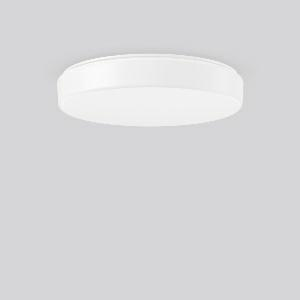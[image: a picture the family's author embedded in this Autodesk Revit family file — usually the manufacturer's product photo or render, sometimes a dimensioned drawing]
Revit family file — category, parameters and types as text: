
# Revit family: flat_polymero_kreis_672392_002_1_ad0b
name_source: partatom
category: Lighting Fixtures
units: mm (PartAtom-declared; Revit-internal decimal feet)

## family parameters
Cut with Voids When Loaded = No
Host = Face
Light Source = No
Part Type = Normal
Room Calculation Point = No
Round Connector Dimension = Use Diameter
Shared = No

## types (1)
- FLAT POLYMERO KREIS (1 x LED Modul 840, 2600 lm, 4000)
    Apparent Load = 23 VA
    CIE Flux Codes = 42 72 91 84 100
    Color Rendering = 80
    Color Temperature = 4000
    Default Elevation = 1800 mm
    Description = Series: FLAT POLYMERO KREIS
Decorative round surface-mounted luminaire. For escape route illumination. Base: metal, powder-coated. Diffuser made of non-yellowing plastic (PMMA), opal. Diffuser fastening: patented push system. Suitable for Ceiling mounting, Wall (surface). Driver integrated. Suitable for connection to central battery systems. 
Colour: white
Diameter: 515 mm
Height: 98 mm
Weight: 2.8 kg
Operating mode: Combined NL readiness
Lamp: LED
Socket: without socket
Colour temperature: 4000K
Colour rendering index (CRI): 80
System power: 23 W
Rated luminous flux: 2600 lm
Luminous flux, emergency: 550 lm
System power, emergency: 5.9 W
Control gear: Regulated power supply
Protection class: I
Type of protection: IP 40
    Height = 98 mm
    Lamp = 1 x LED Modul 840
    Lamp Light Flux = 2600 lm
    Lamp count = 1
    Length = 515 mm
    Lifetime = 50000 h
    Luminous efficacy = 113 lm/W
    Manufacturer = RZB
    ModVariant = No
    Model = 672392.002.1
    Mounting Place = Ceiling, Wall
    Mounting Type = Surface mounted
    Number of Poles = 1
    OnlyDefault = Yes
    Power Factor = 1
    Product Name = FLAT POLYMERO KREIS
    Product group = Surface mounted ceiling and wall luminaires
    ProductGroupID = 305
    Protection Class = Protection class I
    Protection Degree = IP 40
    RLX_Detail_Level = 1
    RLX_Emergency_Light_Flux = 550 lm
    RLX_Emergency_Type = 3
    RLX_Emergency_Type_DB = Yes
    RlxData = <blob elided: 56909 chars, md5=1ab95a3c>
    Socket = socket
    Standby Power = 0 W
    System Light Flux = 2600 lm
    System Power = 23 W
    Type Comments = Product without accessories
    Type Image = 311604.862.79.jpg
    URL = http://relux.com
    VarID = ---
    Voltage = 230 V
    Voltage Range = 220-240 V
    Weight = 0.00 kg
    Width = 0 mm  [stored 0 ft]

note: [stored X ft] marks values corroborated as IEEE doubles in the binary element streams (Revit-internal decimal feet)

## geometry (parser evidence)
native form markers: Blend x4, Sweep x15
no freeform markers — native parametric forms only
